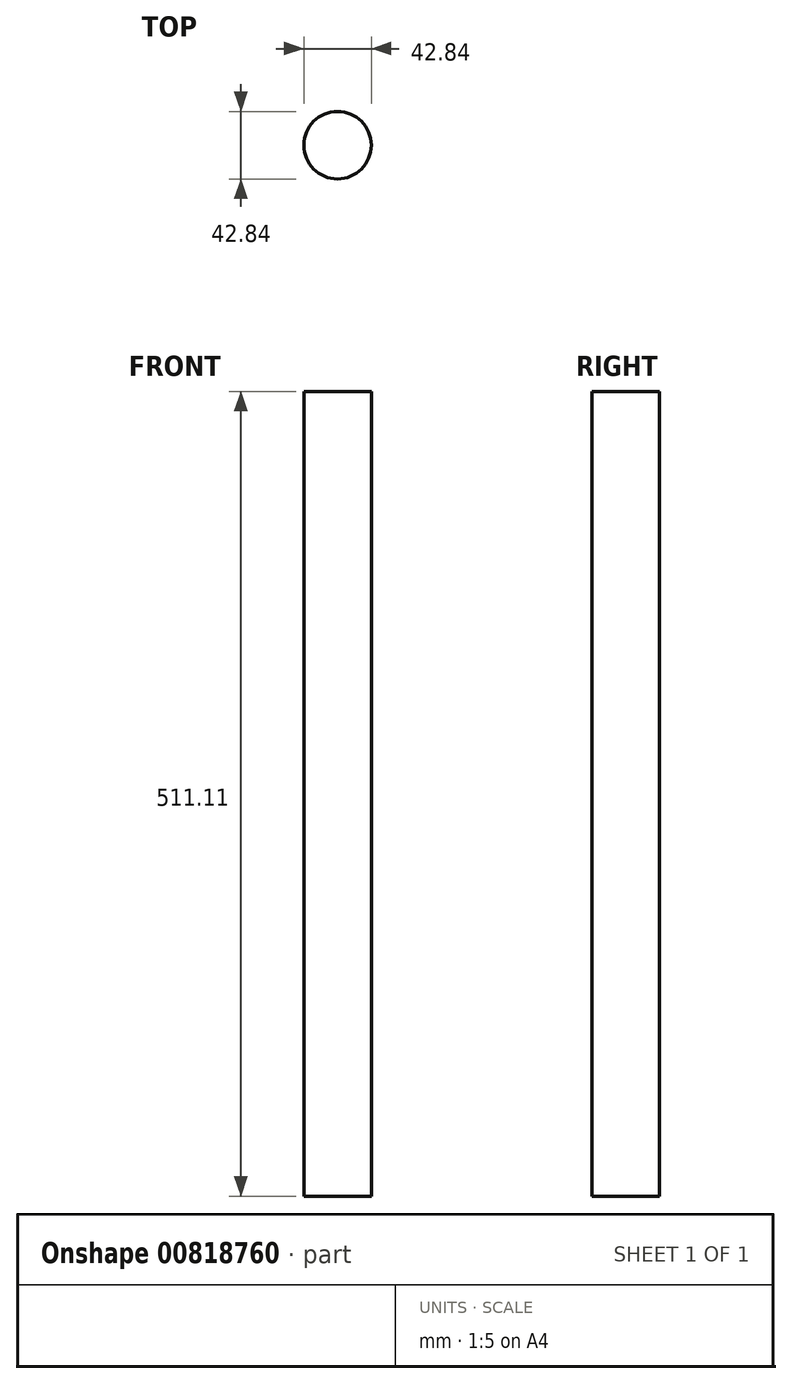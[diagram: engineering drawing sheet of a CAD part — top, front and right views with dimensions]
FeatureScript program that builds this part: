
annotation { "Feature Type Name" : "Feature", "Feature Type Description" : "" }
export const myFeature = defineFeature(function(context is Context, id is Id, definition is map)
    precondition{}
    {
        {
            var Q0;
            Q0=qCreatedBy(makeId("Top.planeOp"),FACE);
            var sketch = newSketch(context, id + "F0", { "sketchPlane" : qUnion([Q0])});
            skCircle(sketch, "E0", {"center": v(51.39, -54.38) * mm, "radius": 21.42 * mm});
            skSolve(sketch);
        }
        {
            var Q0;
            Q0=makeQuery(id+"F0.imprint","IMPRINT",FACE,{"disambiguationData":[TD([[makeQuery(id+"F0.imprint","IMPRINT",EDGE,{"derivedFrom":sQuery(id+"F0.wireOp",EDGE,"E0")}),1.0]])]});
            extrude(context, id + "F1", {"entities" : qUnion([Q0]), "depth" : 511.1 * mm, "offsetDistance" : 25.4 * mm});
        }
    });
